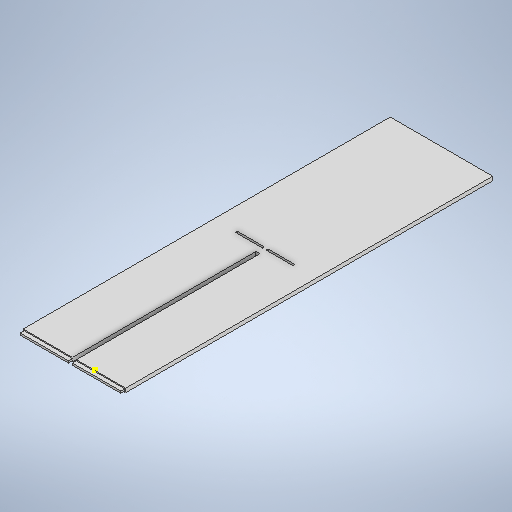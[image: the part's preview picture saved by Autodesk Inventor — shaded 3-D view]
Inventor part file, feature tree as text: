
AUTODESK INVENTOR PART (.ipt)
format: ipt  version: 2025.2 (Build 292293000, 293)  size: 381,440 bytes
history: native  units: mm
features: sketch x13, extrude x12, projected_geometry x3
ambient origin geometry x8: Origin, YZ Plane, XZ Plane, XY Plane, X Axis, Y Axis, Z Axis, Center Point
bodies: Solid1 (feature_tree)
feature tree (28):
  extrude  "Extrusion1"  Depth=447.675mm
  extrude  "Extrusion2"  Depth=4.7625mm TaperAngle=0.0deg
  extrude  "Extrusion3"  Depth=10.0mm TaperAngle=0.0deg
  extrude  "Extrusion4"  Depth=158.838mm TaperAngle=0.0deg
  sketch  "Sketch5"  dims[d25=4.763mm d26=223.837mm d27=0.0mm]
  extrude  "Extrusion5"  Depth=223.837mm TaperAngle=0.0deg
  extrude  "Extrusion6"  Depth=15.0mm TaperAngle=0.0deg
  extrude  "Extrusion7"  Depth=2.374mm TaperAngle=0.0deg
  extrude  "Extrusion8"  Depth=37.5mm
  extrude  "Extrusion9"  Depth=10.0mm TaperAngle=0.0deg
  extrude  "Extrusion10"  Depth=32.503mm TaperAngle=0.0deg
  extrude  "Extrusion11"  [1 undecoded]
  extrude  "Extrusion12"  [1 undecoded]
  sketch  "Sketch1"  dims[d0=50.0mm d1=447.675mm]
  sketch  "Sketch2"  dims[d2=4.7625mm d3=0.0mm d9=4.7625mm d10=0.0mm]
  sketch  "Sketch3"  dims[d11=25.0mm d18=10.0mm d19=0.0mm]
  sketch  "Sketch4"  dims[d20=10.0mm d21=0.0mm d22=158.838mm d23=0.0mm]
  sketch  "Sketch6"  dims[d28=15.0mm d29=0.0mm d30=15.0mm d31=0.0mm]
  projected_geometry  "Projected Loop1"
  sketch  "Sketch8"  dims[d35=2.374mm d36=10.0mm d37=0.0mm]
  sketch  "Sketch9"  dims[d39=37.5mm d40=37.5mm]
  projected_geometry  "Projected Loop2"
  sketch  "Sketch10"  dims[d41=10.0mm d42=0.0mm d44=10.0mm d45=0.0mm]
  projected_geometry  "Projected Loop3"
  sketch  "Sketch14"  dims[d47=32.503mm d48=10.0mm d49=0.0mm]
  sketch  "Sketch17"
  sketch  "Sketch18"
  sketch  "Sketch19"
note: 2 required parameter values undecoded (feature->parameter linkage not recoverable at this tier; creation-order binding heuristic only, values carry confidence <= 0.55)
